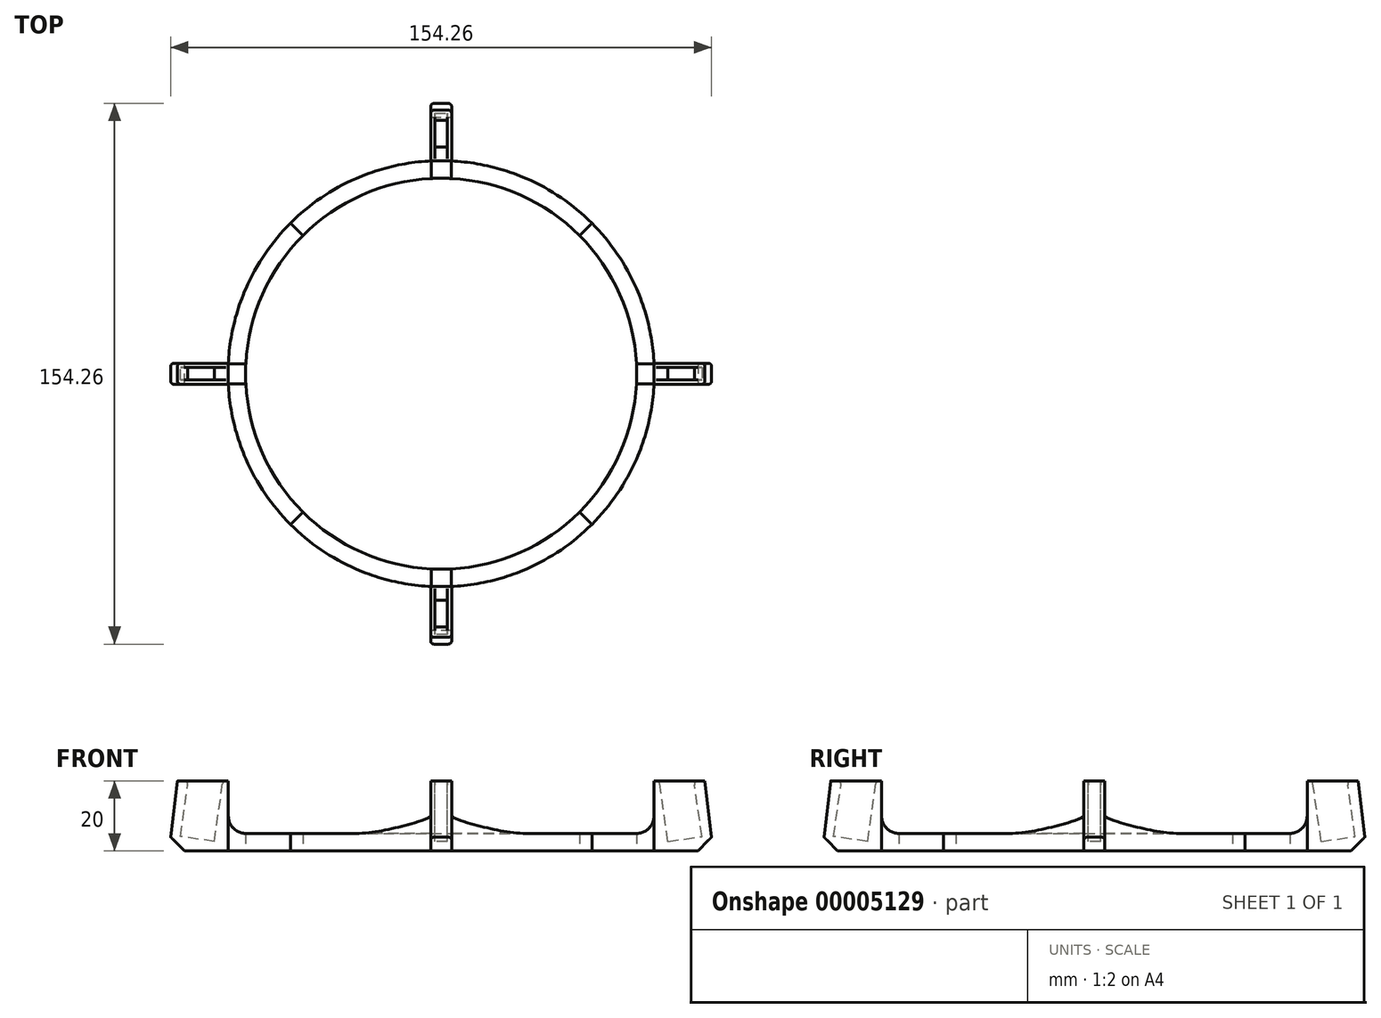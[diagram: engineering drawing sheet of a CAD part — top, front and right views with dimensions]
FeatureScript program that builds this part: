
annotation { "Feature Type Name" : "Feature", "Feature Type Description" : "" }
export const myFeature = defineFeature(function(context is Context, id is Id, definition is map)
    precondition{}
    {
        {
            var Q0;
            Q0=qCreatedBy(makeId("Front.planeOp"),FACE);
            var sketch = newSketch(context, id + "F0", { "sketchPlane" : qUnion([Q0])});
            skLineSegment(sketch, "E0", {"start": v(0, 0) * mm, "end": v(-70, 0) * mm, "construction": true});
            skLineSegment(sketch, "E1", {"start": v(0, 0) * mm, "end": v(0, 140) * mm, "construction": true});
            skLineSegment(sketch, "E2", {"start": v(0, 140) * mm, "end": v(-50, 140) * mm, "construction": true});
            skLineSegment(sketch, "E3", {"start": v(-70, 0) * mm, "end": v(-50, 140) * mm, "construction": true});
            skPoint(sketch, "E4", {"position": v(-63.64, 44.55) * mm});
            skSolve(sketch);
        }
        {
            var Q0;
            Q0=qCreatedBy(makeId("Top.planeOp"),FACE);
            var sketch = newSketch(context, id + "F1", { "sketchPlane" : qUnion([Q0])});
            skArc(sketch, "E5", {"start": v(-39.44, 39.44) * mm, "mid": v(-55.77, 0) * mm, "end": v(-39.44, -39.44) * mm});
            skArc(sketch, "E6", {"start": v(-42.97, 42.97) * mm, "mid": v(-60.77, 0) * mm, "end": v(-42.97, -42.97) * mm});
            skLineSegment(sketch, "E7", {"start": v(0, 0) * mm, "end": v(-39.44, -39.44) * mm, "construction": true});
            skLineSegment(sketch, "E8", {"start": v(-39.44, -39.44) * mm, "end": v(-42.97, -42.97) * mm});
            skLineSegment(sketch, "E9", {"start": v(0, 0) * mm, "end": v(-39.44, 39.44) * mm, "construction": true});
            skLineSegment(sketch, "E10", {"start": v(-39.44, 39.44) * mm, "end": v(-42.97, 42.97) * mm});
            skLineSegment(sketch, "E11", {"start": v(0, 0) * mm, "end": v(-55.77, 0) * mm, "construction": true});
            skSolve(sketch);
        }
        {
            var Q0;
            Q0 = qSketchRegion(id + "F1", true);
            extrude(context, id + "F2", {"entities" : qUnion([Q0]), "depth" : 5 * mm});
        }
        {
            var Q0;
            Q0=qCreatedBy(makeId("Top.planeOp"),FACE);
            var sketch = newSketch(context, id + "F3", { "sketchPlane" : qUnion([Q0])});
            skLineSegment(sketch, "E12.bottom", {"start": v(-60.7, 3) * mm, "end": v(-78.2, 3) * mm});
            skLineSegment(sketch, "E12.top", {"start": v(-60.7, -3) * mm, "end": v(-78.2, -3) * mm});
            skLineSegment(sketch, "E12.left", {"start": v(-60.7, 3) * mm, "end": v(-60.7, -3) * mm});
            skLineSegment(sketch, "E12.right", {"start": v(-78.2, 3) * mm, "end": v(-78.2, -3) * mm});
            skLineSegment(sketch, "E13", {"start": v(-60.7, 0) * mm, "end": v(0, 0) * mm, "construction": true});
            skSolve(sketch);
        }
        {
            var Q0;
            Q0 = qSketchRegion(id + "F3", true);
            extrude(context, id + "F4", {"entities" : qUnion([Q0]), "operationType" : NewBodyOperationType.ADD, "depth" : 20 * mm});
        }
        {
            var Q0;
            Q0=makeQuery(id+"F4.boolean.opBoolean","INTERSECT",EDGE,{"derivedFrom":[makeQuery(id+"F2.opExtrude","CAP_FACE",FACE,{"disambiguationData":[OSD([sQuery(id+"F1.wireOp",EDGE,"E5"),sQuery(id+"F1.wireOp",EDGE,"E6")])],"isStart":false}),makeQuery(id+"F4.opExtrude","SWEPT_FACE",FACE,{"disambiguationData":[OSD([sQuery(id+"F3.wireOp",EDGE,"E12.left")])]})]});
            fillet(context, id + "F5", {"entities" : qUnion([Q0]), "radius" : 5 * mm, "tangentPropagation" : true, "allowEdgeOverflow" : false});
        }
        {
            var Q0;
            Q0=sQuery(id+"F0.wireOp",EDGE,"E3");
            var Q1;
            Q1=sQuery(id+"F0.wireOp",VERTEX,"E4");
            cPlane(context, id + "F6", {"entities" : qUnion([Q0, Q1]), "cplaneType" : CPlaneType.LINE_POINT, "offset" : 150 * mm, "width" : 150 * mm, "height" : 150 * mm});
        }
        {
            var Q0;
            Q0=qCreatedBy(id+"F6.planeOp",FACE);
            var sketch = newSketch(context, id + "F7", { "sketchPlane" : qUnion([Q0])});
            skLineSegment(sketch, "E14.bottom", {"start": v(-64.4, -1.75) * mm, "end": v(-74.2, -1.75) * mm});
            skLineSegment(sketch, "E14.top", {"start": v(-64.4, 1.75) * mm, "end": v(-74.2, 1.75) * mm});
            skLineSegment(sketch, "E14.left", {"start": v(-64.4, -1.75) * mm, "end": v(-64.4, 1.75) * mm});
            skLineSegment(sketch, "E14.right", {"start": v(-74.2, -1.75) * mm, "end": v(-74.2, 1.75) * mm});
            skLineSegment(sketch, "E15", {"start": v(-77.7, 0) * mm, "end": v(-64.4, 0) * mm, "construction": true});
            skLineSegment(sketch, "E16", {"start": v(-64.4, 1.75) * mm, "end": v(-74.2, -1.75) * mm, "construction": true});
            skSolve(sketch);
        }
        {
            var Q0;
            Q0 = qSketchRegion(id + "F7", true);
            extrude(context, id + "F8", {"entities" : qUnion([Q0]), "operationType" : NewBodyOperationType.REMOVE, "oppositeDirection" : true, "depth" : 41.55 * mm});
        }
        {
            var Q0;
            Q0=makeQuery(id+"F4.opExtrude","CAP_EDGE",EDGE,{"disambiguationData":[OSD([sQuery(id+"F3.wireOp",EDGE,"E12.right")])],"isStart":true});
            chamfer(context, id + "F9", {"entities" : qUnion([Q0]), "width" : 5 * mm, "tangentPropagation" : true});
        }
        {
            var Q0;
            Q0=makeQuery(id+"F4.opExtrude","CAP_EDGE",EDGE,{"disambiguationData":[OSD([sQuery(id+"F3.wireOp",EDGE,"E12.right")])],"isStart":false});
            chamfer(context, id + "F10", {"entities" : qUnion([Q0]), "chamferType" : ChamferType.TWO_OFFSETS, "width1" : 3 * mm, "oppositeDirection" : false, "width2" : 25 * mm, "tangentPropagation" : true});
        }
        {
            var Q0;
            Q0=makeQuery(id+"F8.boolean.opBoolean","INTERSECT",EDGE,{"derivedFrom":[makeQuery(id+"F4.opExtrude","CAP_FACE",FACE,{"disambiguationData":[OSD([sQuery(id+"F3.wireOp",EDGE,"E12.bottom"),sQuery(id+"F3.wireOp",EDGE,"E12.top"),sQuery(id+"F3.wireOp",EDGE,"E12.left"),sQuery(id+"F3.wireOp",EDGE,"E12.right")])],"isStart":false}),makeQuery(id+"F8.opExtrude","SWEPT_FACE",FACE,{"disambiguationData":[OSD([sQuery(id+"F7.wireOp",EDGE,"E14.right")])]})]});
            var Q1;
            Q1=makeQuery(id+"F8.boolean.opBoolean","INTERSECT",EDGE,{"derivedFrom":[makeQuery(id+"F4.opExtrude","CAP_FACE",FACE,{"disambiguationData":[OSD([sQuery(id+"F3.wireOp",EDGE,"E12.bottom"),sQuery(id+"F3.wireOp",EDGE,"E12.top"),sQuery(id+"F3.wireOp",EDGE,"E12.left"),sQuery(id+"F3.wireOp",EDGE,"E12.right")])],"isStart":false}),makeQuery(id+"F8.opExtrude","SWEPT_FACE",FACE,{"disambiguationData":[OSD([sQuery(id+"F7.wireOp",EDGE,"E14.left")])]})]});
            fillet(context, id + "F11", {"entities" : qUnion([Q0, Q1]), "radius" : 1 * mm, "tangentPropagation" : true, "allowEdgeOverflow" : false});
        }
        {
            var Q0;
            Q0=makeQuery(id+"F10.opChamfer","BLEND_EDGE",EDGE,{"blendedFrom":[makeQuery(id+"F4.opExtrude","CAP_EDGE",EDGE,{"disambiguationData":[OSD([sQuery(id+"F3.wireOp",EDGE,"E12.right")])],"isStart":false}),makeQuery(id+"F4.opExtrude","SWEPT_FACE",FACE,{"disambiguationData":[OSD([sQuery(id+"F3.wireOp",EDGE,"E12.bottom")])]})],"blendedInto":[makeQuery(id+"F4.opExtrude","SWEPT_FACE",FACE,{"disambiguationData":[OSD([sQuery(id+"F3.wireOp",EDGE,"E12.bottom")])]})]});
            var Q1;
            Q1=makeQuery(id+"F10.opChamfer","BLEND_EDGE",EDGE,{"blendedFrom":[makeQuery(id+"F4.opExtrude","CAP_EDGE",EDGE,{"disambiguationData":[OSD([sQuery(id+"F3.wireOp",EDGE,"E12.right")])],"isStart":false}),makeQuery(id+"F4.opExtrude","SWEPT_FACE",FACE,{"disambiguationData":[OSD([sQuery(id+"F3.wireOp",EDGE,"E12.top")])]})],"blendedInto":[makeQuery(id+"F4.opExtrude","SWEPT_FACE",FACE,{"disambiguationData":[OSD([sQuery(id+"F3.wireOp",EDGE,"E12.top")])]})]});
            fillet(context, id + "F12", {"entities" : qUnion([Q0, Q1]), "radius" : 1 * mm, "tangentPropagation" : true, "allowEdgeOverflow" : false});
        }
        {
            var Q0;
            Q0=makeQuery(id+"F2.opExtrude","SWEPT_BODY",BODY,{"disambiguationData":[OSD([sQuery(id+"F1.wireOp",EDGE,"E5"),sQuery(id+"F1.wireOp",EDGE,"E6"),sQuery(id+"F1.wireOp",EDGE,"E8"),sQuery(id+"F1.wireOp",EDGE,"E10")])]});
            var Q1;
            Q1=sQuery(id+"F0.wireOp",EDGE,"E1");
            circularPattern(context, id + "F13", {"entities" : qUnion([Q0]), "axis" : qUnion([Q1]), "angle" : 90 * degree, "instanceCount" : 4});
        }
    });
